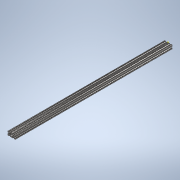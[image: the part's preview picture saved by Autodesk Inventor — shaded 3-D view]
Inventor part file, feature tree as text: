
AUTODESK INVENTOR PART (.ipt)
format: ipt  version: 2020 (Build 240168000, 168)  size: 365,568 bytes
history: native  units: in
note: dims shown in document units (in); Inventor stores cm internally (conversion verified against a paired STEP export)
features: sketch x2, extrude x1
ambient origin geometry x8: Origin, YZ Plane, XZ Plane, XY Plane, X Axis, Y Axis, Z Axis, Center Point
bodies: Solid1 (feature_tree)
feature tree (3):
  extrude  "Extrusion1"  [1 undecoded]
  sketch  "Sketch2"
  sketch  "Sketch1"  dims[d0=40.0in d1=0.0in]
note: 1 required parameter value undecoded (feature->parameter linkage not recoverable at this tier; creation-order binding heuristic only, values carry confidence <= 0.55)
